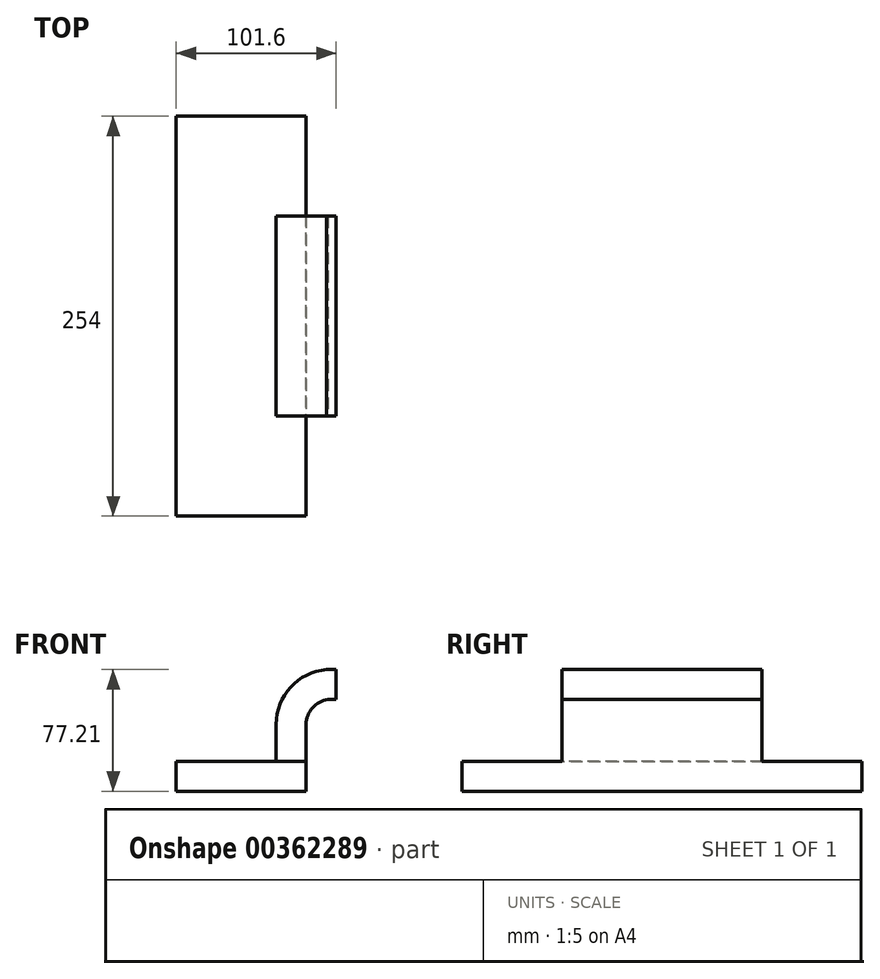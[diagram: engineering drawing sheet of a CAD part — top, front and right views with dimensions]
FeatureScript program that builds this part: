
annotation { "Feature Type Name" : "Feature", "Feature Type Description" : "" }
export const myFeature = defineFeature(function(context is Context, id is Id, definition is map)
    precondition{}
    {
        {
            var Q0;
            Q0=qCreatedBy(makeId("Front.planeOp"),FACE);
            var sketch = newSketch(context, id + "F0", { "sketchPlane" : qUnion([Q0])});
            skLineSegment(sketch, "E0.bottom", {"start": v(41.28, -9.52) * mm, "end": v(-41.28, -9.53) * mm});
            skLineSegment(sketch, "E0.top", {"start": v(41.28, 9.53) * mm, "end": v(-41.28, 9.53) * mm});
            skLineSegment(sketch, "E0.left", {"start": v(41.28, -9.52) * mm, "end": v(41.28, 9.53) * mm});
            skLineSegment(sketch, "E0.right", {"start": v(-41.28, -9.53) * mm, "end": v(-41.28, 9.53) * mm});
            skPoint(sketch, "E0.middle", {"position": v(0, 0) * mm});
            skLineSegment(sketch, "E1.bottom", {"start": v(111.12, 42.88) * mm, "end": v(60.32, 42.88) * mm});
            skLineSegment(sketch, "E1.top", {"start": v(111.12, 71.45) * mm, "end": v(60.32, 71.45) * mm});
            skLineSegment(sketch, "E1.left", {"start": v(111.12, 42.88) * mm, "end": v(111.12, 71.45) * mm});
            skLineSegment(sketch, "E1.right", {"start": v(60.32, 42.88) * mm, "end": v(60.32, 71.45) * mm});
            skPoint(sketch, "E1.middle", {"position": v(85.72, 57.16) * mm});
            skLineSegment(sketch, "E2", {"start": v(41.28, 9.53) * mm, "end": v(41.28, 32.88) * mm});
            skArc(sketch, "E3", {"start": v(41.28, 32.88) * mm, "mid": v(45.25, 43.39) * mm, "end": v(55.19, 48.63) * mm});
            skLineSegment(sketch, "E4", {"start": v(55.19, 48.63) * mm, "end": v(87.03, 48.63) * mm});
            skLineSegment(sketch, "E5.0", {"start": v(54.24, 67.68) * mm, "end": v(85.72, 67.68) * mm});
            skArc(sketch, "E5.1", {"start": v(22.23, 32.88) * mm, "mid": v(31.44, 56.52) * mm, "end": v(54.24, 67.68) * mm});
            skLineSegment(sketch, "E6", {"start": v(22.23, 32.88) * mm, "end": v(22.23, 9.53) * mm});
            skSolve(sketch);
        }
        {
            var Q0;
            Q0=qCreatedBy(makeId("Front.planeOp"),FACE);
            var sketch = newSketch(context, id + "F1", { "sketchPlane" : qUnion([Q0])});
            skFitSpline(sketch, "E7", {"points": [v(-41.38, 9.55) * mm, v(54.11, 67.88) * mm], "startDerivative": vector(1.55, 124.66) * mm, "endDerivative": vector(154.86, 1.55) * mm});
            skSolve(sketch);
        }
        {
            var Q0;
            Q0 = qSketchRegion(id + "F1", true);
            var Q1;
            Q1=makeQuery(id+"F0.imprint","IMPRINT",FACE,{"disambiguationData":[TD([[makeQuery(id+"F0.imprint","IMPRINT",EDGE,{"derivedFrom":sQuery(id+"F0.wireOp",EDGE,"E0.bottom")}),-1.0]])]});
            extrude(context, id + "F2", {"entities" : qUnion([Q0, Q1]), "endBound" : BoundingType.SYMMETRIC, "depth" : 127 * mm});
        }
        {
            var Q0;
            {var subQ1=sQuery(id+"F0.wireOp",EDGE,"E2");Q0=makeQuery(id+"F0.imprint","IMPRINT",FACE,{"disambiguationData":[TD([[makeQuery(id+"F0.imprint","IMPRINT",EDGE,{"derivedFrom":subQ1}),1.0]])]});}
            var Q1;
            Q1=makeQuery(id+"F2.opExtrude","CAP_FACE",FACE,{"disambiguationData":[OSD([sQuery(id+"F0.wireOp",EDGE,"E0.bottom"),sQuery(id+"F0.wireOp",EDGE,"E0.top"),sQuery(id+"F0.wireOp",EDGE,"E0.left"),sQuery(id+"F0.wireOp",EDGE,"E0.right")])],"isStart":false});
            var Q2;
            Q2=makeQuery(id+"F2.opExtrude","CAP_FACE",FACE,{"disambiguationData":[OSD([sQuery(id+"F0.wireOp",EDGE,"E0.bottom"),sQuery(id+"F0.wireOp",EDGE,"E0.top"),sQuery(id+"F0.wireOp",EDGE,"E0.left"),sQuery(id+"F0.wireOp",EDGE,"E0.right")])],"isStart":true});
            extrude(context, id + "F3", {"entities" : qUnion([Q0, Q1, Q2]), "operationType" : NewBodyOperationType.ADD, "endBound" : BoundingType.SYMMETRIC, "oppositeDirection" : true, "depth" : 127 * mm});
        }
    });
